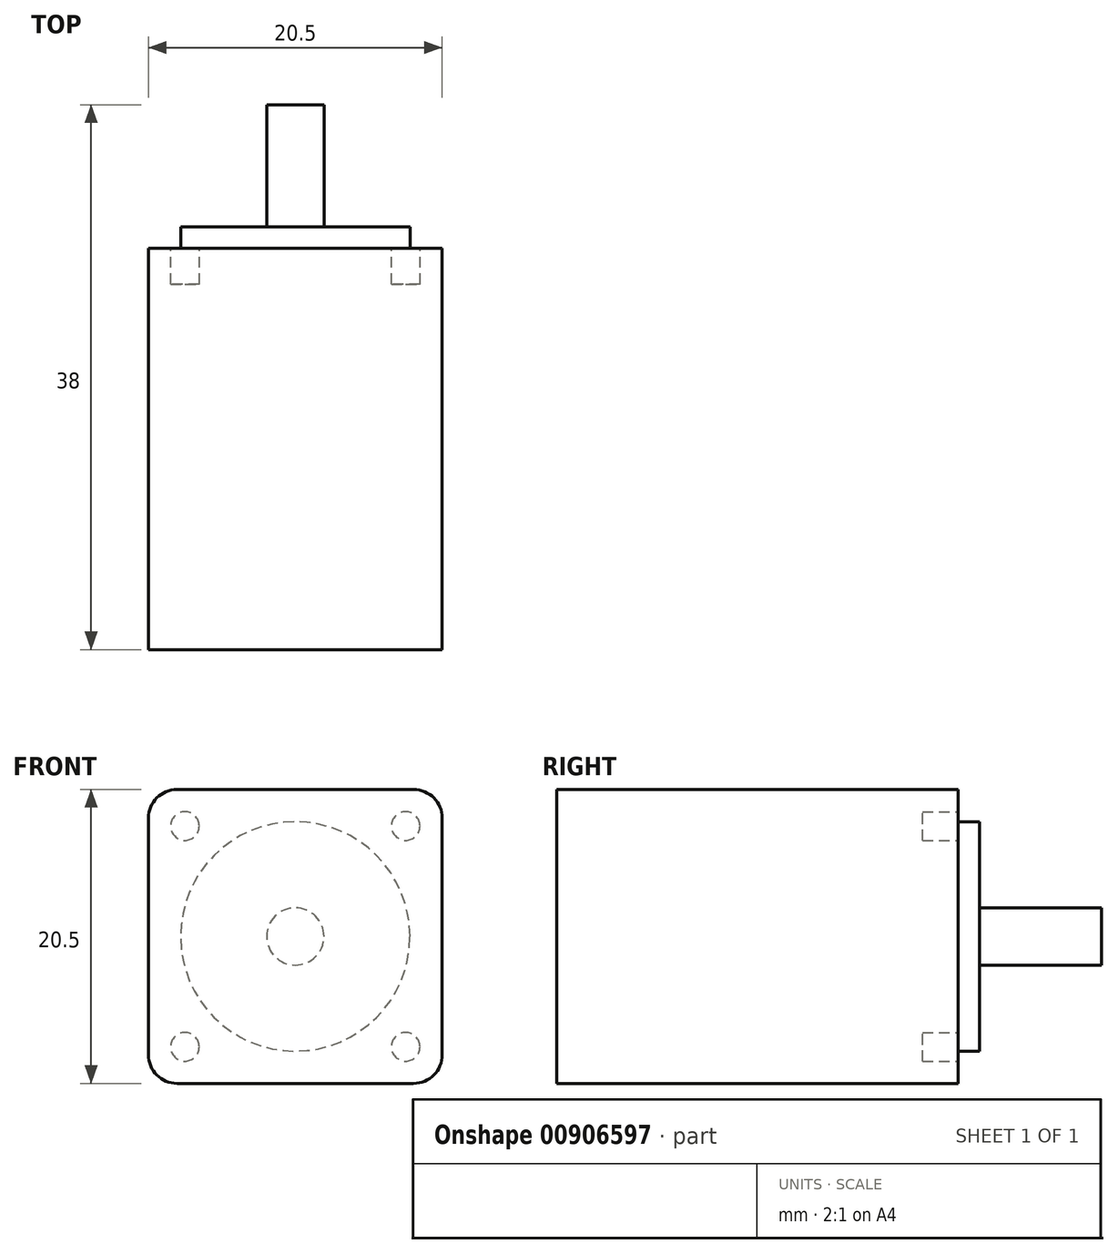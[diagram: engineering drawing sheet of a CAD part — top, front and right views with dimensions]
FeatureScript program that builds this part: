
annotation { "Feature Type Name" : "Feature", "Feature Type Description" : "" }
export const myFeature = defineFeature(function(context is Context, id is Id, definition is map)
    precondition{}
    {
        {
            var Q0;
            Q0=qCreatedBy(makeId("Front.planeOp"),FACE);
            var sketch = newSketch(context, id + "F0", { "sketchPlane" : qUnion([Q0])});
            skLineSegment(sketch, "E0.bottom", {"start": v(-8.25, 10.25) * mm, "end": v(8.25, 10.25) * mm});
            skLineSegment(sketch, "E0.top", {"start": v(-8.25, -10.25) * mm, "end": v(8.25, -10.25) * mm});
            skLineSegment(sketch, "E0.left", {"start": v(-10.25, 8.25) * mm, "end": v(-10.25, -8.25) * mm});
            skLineSegment(sketch, "E0.right", {"start": v(10.25, 8.25) * mm, "end": v(10.25, -8.25) * mm});
            skPoint(sketch, "E0.middle", {"position": v(0, 0) * mm});
            skLineSegment(sketch, "E1.bottom", {"start": v(-7.7, 7.7) * mm, "end": v(7.7, 7.7) * mm});
            skLineSegment(sketch, "E1.top", {"start": v(-7.7, -7.7) * mm, "end": v(7.7, -7.7) * mm});
            skLineSegment(sketch, "E1.left", {"start": v(-7.7, 7.7) * mm, "end": v(-7.7, -7.7) * mm});
            skLineSegment(sketch, "E1.right", {"start": v(7.7, 7.7) * mm, "end": v(7.7, -7.7) * mm});
            skCircle(sketch, "E2", {"center": v(-7.7, 7.7) * mm, "radius": 1 * mm});
            skCircle(sketch, "E3", {"center": v(7.7, 7.7) * mm, "radius": 1 * mm});
            skCircle(sketch, "E4", {"center": v(7.7, -7.7) * mm, "radius": 1 * mm});
            skCircle(sketch, "E5", {"center": v(-7.7, -7.7) * mm, "radius": 1 * mm});
            skPoint(sketch, "E6.visualSharp", {"position": v(10.25, 10.25) * mm});
            skArc(sketch, "E6.filletArc", {"start": v(10.25, 8.25) * mm, "mid": v(9.66, 9.66) * mm, "end": v(8.25, 10.25) * mm});
            skPoint(sketch, "E7.visualSharp", {"position": v(10.25, -10.25) * mm});
            skArc(sketch, "E7.filletArc", {"start": v(8.25, -10.25) * mm, "mid": v(9.66, -9.66) * mm, "end": v(10.25, -8.25) * mm});
            skPoint(sketch, "E8.visualSharp", {"position": v(-10.25, -10.25) * mm});
            skArc(sketch, "E8.filletArc", {"start": v(-10.25, -8.25) * mm, "mid": v(-9.66, -9.66) * mm, "end": v(-8.25, -10.25) * mm});
            skPoint(sketch, "E9.visualSharp", {"position": v(-10.25, 10.25) * mm});
            skArc(sketch, "E9.filletArc", {"start": v(-8.25, 10.25) * mm, "mid": v(-9.66, 9.66) * mm, "end": v(-10.25, 8.25) * mm});
            skSolve(sketch);
        }
        {
            var Q0;
            Q0 = qSketchRegion(id + "F0", true);
            var Q1;
            {var subQ5=sQuery(id+"F0.wireOp",EDGE,"E2");var subQ13=sQuery(id+"F0.wireOp",EDGE,"E1.bottom");var subQ14=makeQuery(id+"F0.imprint","INTERSECT",VERTEX,{"derivedFrom":[subQ13,subQ5]});Q1=makeQuery(id+"F0.imprint","IMPRINT",FACE,{"disambiguationData":[TD([[makeQuery(id+"F0.imprint","IMPRINT",EDGE,{"disambiguationData":[TD([[subQ14,-1.0]])],"derivedFrom":subQ13}),-1.0]])]});}
            extrude(context, id + "F1", {"entities" : qUnion([Q0, Q1]), "depth" : 28 * mm, "offsetDistance" : 25.4 * mm});
        }
        {
            var Q0;
            Q0=makeQuery(id+"F1.opExtrude","CAP_FACE",FACE,{"disambiguationData":[OSD([sQuery(id+"F0.wireOp",EDGE,"E0.bottom"),sQuery(id+"F0.wireOp",EDGE,"E0.top"),sQuery(id+"F0.wireOp",EDGE,"E0.left"),sQuery(id+"F0.wireOp",EDGE,"E0.right"),sQuery(id+"F0.wireOp",EDGE,"E2"),sQuery(id+"F0.wireOp",EDGE,"E3"),sQuery(id+"F0.wireOp",EDGE,"E4"),sQuery(id+"F0.wireOp",EDGE,"E5"),sQuery(id+"F0.wireOp",EDGE,"E6.filletArc"),sQuery(id+"F0.wireOp",EDGE,"E7.filletArc"),sQuery(id+"F0.wireOp",EDGE,"E8.filletArc"),sQuery(id+"F0.wireOp",EDGE,"E9.filletArc")])],"isStart":false});
            var sketch = newSketch(context, id + "F2", { "sketchPlane" : qUnion([Q0])});
            skCircle(sketch, "E10.0", {"center": v(-7.7, 7.7) * mm, "radius": 1 * mm});
            skCircle(sketch, "E11.0", {"center": v(7.7, 7.7) * mm, "radius": 1 * mm});
            skCircle(sketch, "E12.0", {"center": v(7.7, -7.7) * mm, "radius": 1 * mm});
            skCircle(sketch, "E13.0", {"center": v(-7.7, -7.7) * mm, "radius": 1 * mm});
            skSolve(sketch);
        }
        {
            var Q0;
            Q0 = qSketchRegion(id + "F2", true);
            extrude(context, id + "F3", {"entities" : qUnion([Q0]), "operationType" : NewBodyOperationType.ADD, "oppositeDirection" : true, "depth" : 28 * mm - 2.5 * mm, "offsetDistance" : 25.4 * mm});
        }
        {
            var Q0;
            Q0=makeQuery(id+"F1.opExtrude","SWEPT_FACE",FACE,{"disambiguationData":[OSD([sQuery(id+"F0.wireOp",EDGE,"E0.left")])]});
            cPlane(context, id + "F4", {"entities" : qUnion([Q0]), "cplaneType" : CPlaneType.OFFSET, "offset" : 20.5 / 2 * mm, "oppositeDirection" : true, "width" : 152.4 * mm, "height" : 152.4 * mm});
        }
        {
            var Q0;
            Q0=qCreatedBy(id+"F4.planeOp",FACE);
            var sketch = newSketch(context, id + "F5", { "sketchPlane" : qUnion([Q0])});
            skLineSegment(sketch, "E14", {"start": v(0, 0) * mm, "end": v(-10, 0) * mm});
            skLineSegment(sketch, "E15", {"start": v(-10, 0) * mm, "end": v(-10, 2) * mm});
            skLineSegment(sketch, "E16", {"start": v(-10, 2) * mm, "end": v(-1.5, 2) * mm});
            skLineSegment(sketch, "E17", {"start": v(-1.5, 2) * mm, "end": v(-1.5, 8) * mm});
            skLineSegment(sketch, "E18", {"start": v(-1.5, 8) * mm, "end": v(0, 8) * mm});
            skLineSegment(sketch, "E19", {"start": v(0, 8) * mm, "end": v(0, 0) * mm});
            skSolve(sketch);
        }
        {
            var Q0;
            Q0 = qSketchRegion(id + "F5", true);
            var Q1;
            Q1=sQuery(id+"F5.wireOp",EDGE,"E14");
            revolve(context, id + "F6", {"operationType" : NewBodyOperationType.ADD, "surfaceOperationType" : NewSurfaceOperationType.NEW, "entities" : qUnion([Q0]), "axis" : qUnion([Q1]), "revolveType" : RevolveType.FULL});
        }
    });
